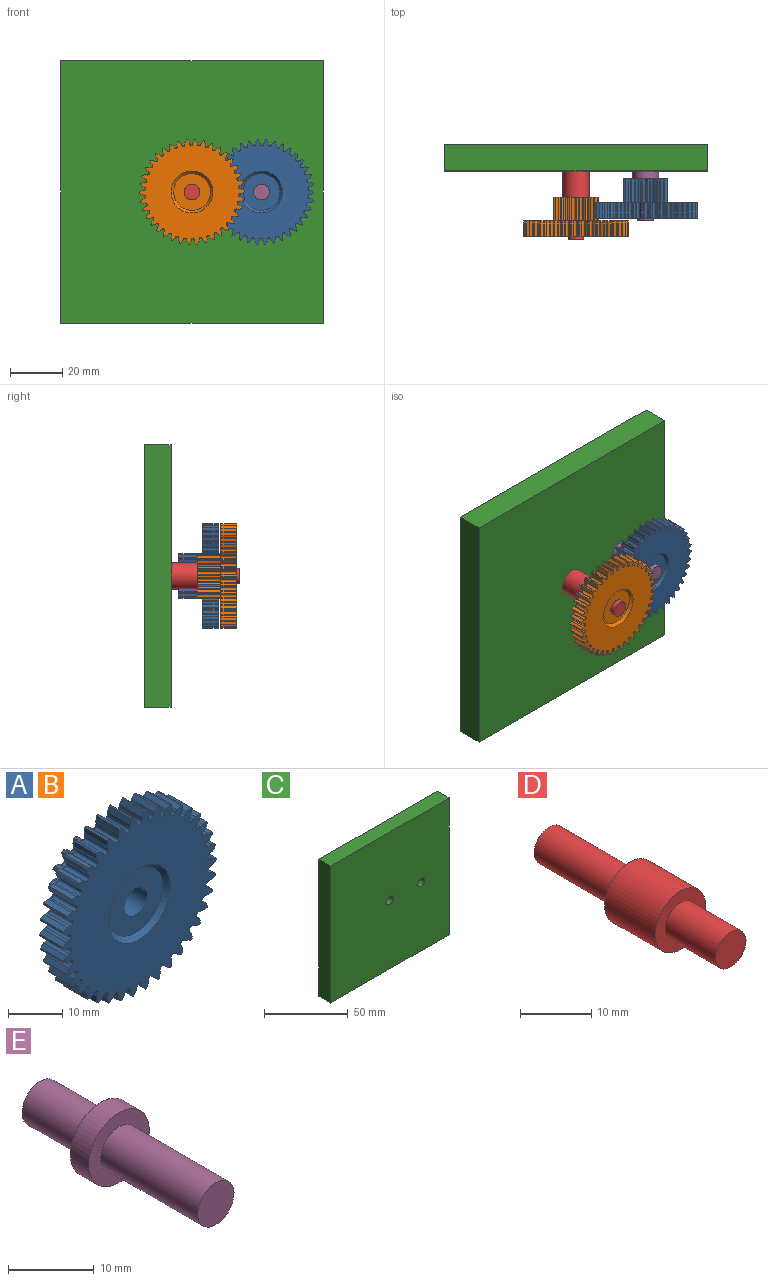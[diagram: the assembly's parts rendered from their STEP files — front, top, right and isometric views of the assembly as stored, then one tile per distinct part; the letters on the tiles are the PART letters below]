
ASSEMBLY  parts=5 mates=4
PART A: 326 faces, bbox 40x15x39.9 mm
  f0: plane 5x0.06mm, normal (-1,0,0), area 0.3mm2, adj f1,f3,f324
  f1: cylinder r=0.62mm len=5mm, axis (0,1,0), area 0.3mm2, adj f0,f3,f324
  f2: cylinder r=3mm len=14mm, axis (0,1,0), area 263.9mm2, adj f323,f324
  f3: plane 40x39.9mm, normal (0,1,0), area 943.4mm2, adj f0,f1,f4,f5,f6,f7,f8,f9
  f4: plane 6x0.6mm, normal (-0.33,0,-0.94), area 3.8mm2, adj f3,f5,f231,f232
  f5: cylinder r=0.62mm len=6mm, axis (0,1,0), area 11.7mm2, adj f3,f4,f6,f232
  f6: plane 6x0.63mm, normal (-0.19,0,0.98), area 3.9mm2, adj f3,f5,f7,f232
  f7: plane 6x1.02mm, normal (-0.51,0,0.86), area 7.1mm2, adj f3,f6,f8,f232
  f8: cylinder r=20mm len=6mm, axis (0,1,0), area 2.3mm2, adj f3,f7,f9,f232
  f9: plane 6x1.02mm, normal (-0.5,0,-0.87), area 7mm2, adj f3,f8,f10,f232
  f10: plane 6x0.63mm, normal (-0.17,0,-0.99), area 3.8mm2, adj f3,f9,f11,f232
  f11: cylinder r=0.62mm len=6mm, axis (0,1,0), area 11.7mm2, adj f3,f10,f12,f232
  f12: plane 6x0.6mm, normal (-0.35,0,0.94), area 3.9mm2, adj f3,f11,f13,f232
  f13: plane 6x0.9mm, normal (-0.65,0,0.76), area 7.1mm2, adj f3,f12,f14,f232
  f14: cylinder r=20mm len=6mm, axis (0,1,0), area 2.3mm2, adj f3,f13,f15,f232
  f15: plane 6x1.1mm, normal (-0.35,0,-0.94), area 7mm2, adj f3,f14,f16,f232
  f16: plane 6x0.64mm, normal (-0.01,0,-1), area 3.8mm2, adj f3,f15,f17,f232
  f17: cylinder r=0.62mm len=6mm, axis (0,1,0), area 11.7mm2, adj f3,f16,f18,f232
  f18: plane 6x0.56mm, normal (-0.5,0,0.87), area 3.9mm2, adj f3,f17,f19,f232
  f19: plane 6x0.9mm, normal (-0.76,0,0.65), area 7.1mm2, adj f3,f18,f20,f232
  f20: cylinder r=20mm len=6mm, axis (0,1,0), area 2.3mm2, adj f3,f19,f21,f232
  f21: plane 6x1.15mm, normal (-0.19,0,-0.98), area 7mm2, adj f3,f20,f22,f232
  f22: plane 6x0.63mm, normal (0.16,0,-0.99), area 3.8mm2, adj f3,f21,f23,f232
  f23: cylinder r=0.62mm len=6mm, axis (0,1,0), area 11.7mm2, adj f3,f22,f24,f232
  f24: plane 6x0.5mm, normal (-0.63,0,0.78), area 3.9mm2, adj f3,f23,f25,f232
  f25: plane 6x1.01mm, normal (-0.86,0,0.51), area 7.1mm2, adj f3,f24,f26,f232
  f26: cylinder r=20mm len=6mm, axis (0,1,0), area 2.3mm2, adj f3,f25,f27,f232
  f27: plane 6x1.17mm, normal (-0.02,0,-1), area 7mm2, adj f3,f26,f28,f232
  f28: plane 6x0.61mm, normal (0.32,0,-0.95), area 3.8mm2, adj f3,f27,f29,f232
  f29: cylinder r=0.62mm len=6mm, axis (0,1,0), area 11.7mm2, adj f3,f28,f30,f232
  f30: plane 6x0.48mm, normal (-0.75,0,0.66), area 3.9mm2, adj f3,f29,f31,f232
  f31: plane 6x1.1mm, normal (-0.93,0,0.36), area 7.1mm2, adj f3,f30,f32,f232
  f32: cylinder r=20mm len=6mm, axis (0,1,0), area 2.3mm2, adj f3,f31,f33,f232
  f33: plane 6x1.16mm, normal (0.14,0,-0.99), area 7mm2, adj f3,f32,f34,f232
  f34: plane 6x0.56mm, normal (0.47,0,-0.88), area 3.8mm2, adj f3,f33,f35,f232
  f35: cylinder r=0.62mm len=6mm, axis (0,1,0), area 11.7mm2, adj f3,f34,f36,f232
  f36: plane 6x0.55mm, normal (-0.85,0,0.53), area 3.9mm2, adj f3,f35,f37,f232
  f37: plane 6x1.16mm, normal (-0.98,0,0.21), area 7.1mm2, adj f3,f36,f38,f232
  f38: cylinder r=20mm len=6mm, axis (0,1,0), area 2.3mm2, adj f3,f37,f39,f232
  f39: plane 6x1.11mm, normal (0.3,0,-0.95), area 7mm2, adj f3,f38,f40,f232
  f40: plane 6x0.51mm, normal (0.61,0,-0.79), area 3.8mm2, adj f3,f39,f41,f232
  f41: cylinder r=0.62mm len=6mm, axis (0,1,0), area 11.7mm2, adj f3,f40,f42,f232
  f42: plane 6x0.59mm, normal (-0.92,0,0.38), area 3.9mm2, adj f3,f41,f43,f232
  f43: plane 6x1.18mm, normal (-1,0,0.04), area 7.1mm2, adj f3,f42,f44,f232
  f44: cylinder r=20mm len=6mm, axis (0,1,0), area 2.3mm2, adj f3,f43,f45,f232
  f45: plane 6x1.04mm, normal (0.46,0,-0.89), area 7mm2, adj f3,f44,f46,f232
  f46: plane 6x0.47mm, normal (0.73,0,-0.68), area 3.8mm2, adj f3,f45,f47,f232
  f47: cylinder r=0.62mm len=6mm, axis (0,1,0), area 11.7mm2, adj f3,f46,f48,f232
  f48: plane 6x0.63mm, normal (-0.97,0,0.22), area 3.9mm2, adj f3,f47,f49,f232
  f49: plane 6x1.17mm, normal (-0.99,0,-0.12), area 7.1mm2, adj f3,f48,f50,f232
  f50: cylinder r=20mm len=6mm, axis (0,1,0), area 2.3mm2, adj f3,f49,f51,f232
  f51: plane 6x0.94mm, normal (0.6,0,-0.8), area 7mm2, adj f3,f50,f52,f232
  f52: plane 6x0.53mm, normal (0.83,0,-0.55), area 3.8mm2, adj f3,f51,f53,f232
  f53: cylinder r=0.62mm len=6mm, axis (0,1,0), area 11.7mm2, adj f3,f52,f54,f232
  f54: plane 6x0.64mm, normal (-1,0,0.06), area 3.9mm2, adj f3,f53,f55,f232
  f55: plane 6x1.13mm, normal (-0.96,0,-0.28), area 7.1mm2, adj f3,f54,f56,f232
  f56: cylinder r=20mm len=6mm, axis (0,1,0), area 2.3mm2, adj f3,f55,f57,f232
  f57: plane 6x0.84mm, normal (0.72,0,-0.69), area 7mm2, adj f3,f56,f58,f232
  f58: plane 6x0.58mm, normal (0.91,0,-0.41), area 3.8mm2, adj f3,f57,f59,f232
  f59: cylinder r=0.62mm len=6mm, axis (0,1,0), area 11.7mm2, adj f3,f58,f60,f232
  f60: plane 6x0.64mm, normal (-0.99,0,-0.1), area 3.9mm2, adj f3,f59,f61,f232
  f61: plane 6x1.06mm, normal (-0.9,0,-0.44), area 7.1mm2, adj f3,f60,f62,f232
  f62: cylinder r=20mm len=6mm, axis (0,1,0), area 2.3mm2, adj f3,f61,f63,f232
  f63: plane 6x0.96mm, normal (0.82,0,-0.57), area 7mm2, adj f3,f62,f64,f232
  f64: plane 6x0.62mm, normal (0.97,0,-0.25), area 3.8mm2, adj f3,f63,f65,f232
  f65: cylinder r=0.62mm len=6mm, axis (0,1,0), area 11.7mm2, adj f3,f64,f66,f232
  f66: plane 6x0.62mm, normal (-0.96,0,-0.27), area 3.9mm2, adj f3,f65,f67,f232
  f67: plane 6x0.96mm, normal (-0.81,0,-0.58), area 7.1mm2, adj f3,f66,f68,f232
  f68: cylinder r=20mm len=6mm, axis (0,1,0), area 2.3mm2, adj f3,f67,f69,f232
  f69: plane 6x1.06mm, normal (0.91,0,-0.42), area 7mm2, adj f3,f68,f70,f232
  f70: plane 6x0.64mm, normal (1,0,-0.09), area 3.8mm2, adj f3,f69,f71,f232
  f71: cylinder r=0.62mm len=6mm, axis (0,1,0), area 11.7mm2, adj f3,f70,f72,f232
  f72: plane 6x0.58mm, normal (-0.91,0,-0.42), area 3.9mm2, adj f3,f71,f73,f232
  f73: plane 6x0.84mm, normal (-0.71,0,-0.71), area 7.1mm2, adj f3,f72,f74,f232
  f74: cylinder r=20mm len=6mm, axis (0,1,0), area 2.3mm2, adj f3,f73,f75,f232
  f75: plane 6x1.13mm, normal (0.96,0,-0.27), area 7mm2, adj f3,f74,f76,f232
  f76: plane 6x0.64mm, normal (1,0,0.08), area 3.8mm2, adj f3,f75,f77,f232
  f77: cylinder r=0.62mm len=6mm, axis (0,1,0), area 11.7mm2, adj f3,f76,f78,f232
  f78: plane 6x0.53mm, normal (-0.82,0,-0.57), area 3.9mm2, adj f3,f77,f79,f232
  f79: plane 6x0.96mm, normal (-0.58,0,-0.81), area 7.1mm2, adj f3,f78,f80,f232
  f80: cylinder r=20mm len=6mm, axis (0,1,0), area 2.3mm2, adj f3,f79,f81,f232
  f81: plane 6x1.16mm, normal (0.99,0,-0.11), area 7mm2, adj f3,f80,f82,f232
  f82: plane 6x0.62mm, normal (0.97,0,0.24), area 3.8mm2, adj f3,f81,f83,f232
  f83: cylinder r=0.62mm len=6mm, axis (0,1,0), area 11.7mm2, adj f3,f82,f84,f232
  f84: plane 6x0.46mm, normal (-0.72,0,-0.69), area 3.9mm2, adj f3,f83,f85,f232
  f85: plane 6x1.06mm, normal (-0.44,0,-0.9), area 7.1mm2, adj f3,f84,f86,f232
  f86: cylinder r=20mm len=6mm, axis (0,1,0), area 2.3mm2, adj f3,f85,f87,f232
  f87: plane 6x1.17mm, normal (1,0,0.06), area 7mm2, adj f3,f86,f88,f232
  f88: plane 6x0.59mm, normal (0.92,0,0.4), area 3.8mm2, adj f3,f87,f89,f232
  f89: cylinder r=0.62mm len=6mm, axis (0,1,0), area 11.7mm2, adj f3,f88,f90,f232
  f90: plane 6x0.52mm, normal (-0.6,0,-0.8), area 3.9mm2, adj f3,f89,f91,f232
  f91: plane 6x1.13mm, normal (-0.29,0,-0.96), area 7.1mm2, adj f3,f90,f92,f232
  f92: cylinder r=20mm len=6mm, axis (0,1,0), area 2.3mm2, adj f3,f91,f93,f232
  f93: plane 6x1.14mm, normal (0.97,0,0.22), area 7mm2, adj f3,f92,f94,f232
  f94: plane 6x0.54mm, normal (0.84,0,0.54), area 3.8mm2, adj f3,f93,f95,f232
  f95: cylinder r=0.62mm len=6mm, axis (0,1,0), area 11.7mm2, adj f3,f94,f96,f232
  f96: plane 6x0.57mm, normal (-0.46,0,-0.89), area 3.9mm2, adj f3,f95,f97,f232
  f97: plane 6x1.17mm, normal (-0.12,0,-0.99), area 7.1mm2, adj f3,f96,f98,f232
  f98: cylinder r=20mm len=6mm, axis (0,1,0), area 2.3mm2, adj f3,f97,f99,f232
  f99: plane 6x1.08mm, normal (0.92,0,0.38), area 7mm2, adj f3,f98,f100,f232
  f100: plane 6x0.47mm, normal (0.74,0,0.67), area 3.8mm2, adj f3,f99,f101,f232
  f101: cylinder r=0.62mm len=6mm, axis (0,1,0), area 11.7mm2, adj f3,f100,f102,f232
  f102: plane 6x0.61mm, normal (-0.3,0,-0.95), area 3.9mm2, adj f3,f101,f103,f232
  f103: plane 6x1.18mm, normal (0.04,0,-1), area 7.1mm2, adj f3,f102,f104,f232
  f104: cylinder r=20mm len=6mm, axis (0,1,0), area 2.3mm2, adj f3,f103,f105,f232
  f105: plane 6x0.99mm, normal (0.85,0,0.53), area 7mm2, adj f3,f104,f106,f232
  f106: plane 6x0.5mm, normal (0.62,0,0.79), area 3.8mm2, adj f3,f105,f107,f232
  f107: cylinder r=0.62mm len=6mm, axis (0,1,0), area 11.7mm2, adj f3,f106,f108,f232
  f108: plane 6x0.64mm, normal (-0.14,0,-0.99), area 3.9mm2, adj f3,f107,f109,f232
  f109: plane 6x1.16mm, normal (0.2,0,-0.98), area 7.1mm2, adj f3,f108,f110,f232
  f110: cylinder r=20mm len=6mm, axis (0,1,0), area 2.3mm2, adj f3,f109,f111,f232
  f111: plane 6x0.88mm, normal (0.75,0,0.66), area 7mm2, adj f3,f110,f112,f232
  f112: plane 6x0.56mm, normal (0.48,0,0.88), area 3.8mm2, adj f3,f111,f113,f232
  f113: cylinder r=0.62mm len=6mm, axis (0,1,0), area 11.7mm2, adj f3,f112,f114,f232
  f114: plane 6x0.64mm, normal (0.02,0,-1), area 3.9mm2, adj f3,f113,f115,f232
  f115: plane 6x1.1mm, normal (0.36,0,-0.93), area 7.1mm2, adj f3,f114,f116,f232
  f116: cylinder r=20mm len=6mm, axis (0,1,0), area 2.3mm2, adj f3,f115,f117,f232
  f117: plane 6x0.91mm, normal (0.63,0,0.77), area 7mm2, adj f3,f116,f118,f232
  f118: plane 6x0.6mm, normal (0.33,0,0.94), area 3.8mm2, adj f3,f117,f119,f232
  f119: cylinder r=0.62mm len=6mm, axis (0,1,0), area 11.7mm2, adj f3,f118,f120,f232
  f120: plane 6x0.63mm, normal (0.19,0,-0.98), area 3.9mm2, adj f3,f119,f121,f232
  f121: plane 6x1.02mm, normal (0.51,0,-0.86), area 7.1mm2, adj f3,f120,f122,f232
  f122: cylinder r=20mm len=6mm, axis (0,1,0), area 2.3mm2, adj f3,f121,f123,f232
  f123: plane 6x1.02mm, normal (0.5,0,0.87), area 7mm2, adj f3,f122,f124,f232
  f124: plane 6x0.63mm, normal (0.17,0,0.99), area 3.8mm2, adj f3,f123,f125,f232
  f125: cylinder r=0.62mm len=6mm, axis (0,1,0), area 11.7mm2, adj f3,f124,f126,f232
  f126: plane 6x0.6mm, normal (0.35,0,-0.94), area 3.9mm2, adj f3,f125,f127,f232
  f127: plane 6x0.9mm, normal (0.65,0,-0.76), area 7.1mm2, adj f3,f126,f128,f232
  f128: cylinder r=20mm len=6mm, axis (0,1,0), area 2.3mm2, adj f3,f127,f129,f232
  f129: plane 6x1.1mm, normal (0.35,0,0.94), area 7mm2, adj f3,f128,f130,f232
  f130: plane 6x0.64mm, normal (0.01,0,1), area 3.8mm2, adj f3,f129,f131,f232
  f131: cylinder r=0.62mm len=6mm, axis (0,1,0), area 11.7mm2, adj f3,f130,f132,f232
  f132: plane 6x0.56mm, normal (0.5,0,-0.87), area 3.9mm2, adj f3,f131,f133,f232
  f133: plane 6x0.9mm, normal (0.76,0,-0.65), area 7.1mm2, adj f3,f132,f134,f232
  f134: cylinder r=20mm len=6mm, axis (0,1,0), area 2.3mm2, adj f3,f133,f135,f232
  f135: plane 6x1.15mm, normal (0.19,0,0.98), area 7mm2, adj f3,f134,f136,f232
  f136: plane 6x0.63mm, normal (-0.16,0,0.99), area 3.8mm2, adj f3,f135,f137,f232
  f137: cylinder r=0.62mm len=6mm, axis (0,1,0), area 11.7mm2, adj f3,f136,f138,f232
  f138: plane 6x0.5mm, normal (0.63,0,-0.78), area 3.9mm2, adj f3,f137,f139,f232
  f139: plane 6x1.01mm, normal (0.86,0,-0.51), area 7.1mm2, adj f3,f138,f140,f232
  f140: cylinder r=20mm len=6mm, axis (0,1,0), area 2.3mm2, adj f3,f139,f141,f232
  f141: plane 6x1.17mm, normal (0.02,0,1), area 7mm2, adj f3,f140,f142,f232
  f142: plane 6x0.61mm, normal (-0.32,0,0.95), area 3.8mm2, adj f3,f141,f143,f232
  f143: cylinder r=0.62mm len=6mm, axis (0,1,0), area 11.7mm2, adj f3,f142,f144,f232
  f144: plane 6x0.48mm, normal (0.75,0,-0.66), area 3.9mm2, adj f3,f143,f145,f232
  f145: plane 6x1.1mm, normal (0.93,0,-0.36), area 7.1mm2, adj f3,f144,f146,f232
  f146: cylinder r=20mm len=6mm, axis (0,1,0), area 2.3mm2, adj f3,f145,f147,f232
  f147: plane 6x1.16mm, normal (-0.14,0,0.99), area 7mm2, adj f3,f146,f148,f232
  f148: plane 6x0.56mm, normal (-0.47,0,0.88), area 3.8mm2, adj f3,f147,f149,f232
  f149: cylinder r=0.62mm len=6mm, axis (0,1,0), area 11.7mm2, adj f3,f148,f150,f232
  f150: plane 6x0.55mm, normal (0.85,0,-0.53), area 3.9mm2, adj f3,f149,f151,f232
  f151: plane 6x1.16mm, normal (0.98,0,-0.21), area 7.1mm2, adj f3,f150,f152,f232
  f152: cylinder r=20mm len=6mm, axis (0,1,0), area 2.3mm2, adj f3,f151,f153,f232
  f153: plane 6x1.11mm, normal (-0.3,0,0.95), area 7mm2, adj f3,f152,f154,f232
  f154: plane 6x0.51mm, normal (-0.61,0,0.79), area 3.8mm2, adj f3,f153,f155,f232
  f155: cylinder r=0.62mm len=6mm, axis (0,1,0), area 11.7mm2, adj f3,f154,f156,f232
  f156: plane 6x0.59mm, normal (0.92,0,-0.38), area 3.9mm2, adj f3,f155,f157,f232
  f157: plane 6x1.18mm, normal (1,0,-0.04), area 7.1mm2, adj f3,f156,f158,f232
  f158: cylinder r=20mm len=6mm, axis (0,1,0), area 2.3mm2, adj f3,f157,f159,f232
  f159: plane 6x1.04mm, normal (-0.46,0,0.89), area 7mm2, adj f3,f158,f160,f232
  f160: plane 6x0.47mm, normal (-0.73,0,0.68), area 3.8mm2, adj f3,f159,f161,f232
  f161: cylinder r=0.62mm len=6mm, axis (0,1,0), area 11.7mm2, adj f3,f160,f162,f232
  f162: plane 6x0.63mm, normal (0.97,0,-0.22), area 3.9mm2, adj f3,f161,f163,f232
  f163: plane 6x1.17mm, normal (0.99,0,0.12), area 7.1mm2, adj f3,f162,f164,f232
  f164: cylinder r=20mm len=6mm, axis (0,1,0), area 2.3mm2, adj f3,f163,f165,f232
  f165: plane 6x0.94mm, normal (-0.6,0,0.8), area 7mm2, adj f3,f164,f166,f232
  f166: plane 6x0.53mm, normal (-0.83,0,0.55), area 3.8mm2, adj f3,f165,f167,f232
  f167: cylinder r=0.62mm len=6mm, axis (0,1,0), area 11.7mm2, adj f3,f166,f168,f232
  f168: plane 6x0.64mm, normal (1,0,-0.06), area 3.9mm2, adj f3,f167,f169,f232
  f169: plane 6x1.13mm, normal (0.96,0,0.28), area 7.1mm2, adj f3,f168,f170,f232
  f170: cylinder r=20mm len=6mm, axis (0,1,0), area 2.3mm2, adj f3,f169,f171,f232
  f171: plane 6x0.84mm, normal (-0.72,0,0.69), area 7mm2, adj f3,f170,f172,f232
  f172: plane 6x0.58mm, normal (-0.91,0,0.41), area 3.8mm2, adj f3,f171,f173,f232
  f173: cylinder r=0.62mm len=6mm, axis (0,1,0), area 11.7mm2, adj f3,f172,f174,f232
  f174: plane 6x0.64mm, normal (0.99,0,0.1), area 3.9mm2, adj f3,f173,f175,f232
  f175: plane 6x1.06mm, normal (0.9,0,0.44), area 7.1mm2, adj f3,f174,f176,f232
  f176: cylinder r=20mm len=6mm, axis (0,1,0), area 2.3mm2, adj f3,f175,f177,f232
  f177: plane 6x0.96mm, normal (-0.82,0,0.57), area 7mm2, adj f3,f176,f178,f232
  f178: plane 6x0.62mm, normal (-0.97,0,0.25), area 3.8mm2, adj f3,f177,f179,f232
  f179: cylinder r=0.62mm len=6mm, axis (0,1,0), area 11.7mm2, adj f3,f178,f180,f232
  f180: plane 6x0.62mm, normal (0.96,0,0.27), area 3.9mm2, adj f3,f179,f181,f232
  f181: plane 6x0.96mm, normal (0.81,0,0.58), area 7.1mm2, adj f3,f180,f182,f232
  f182: cylinder r=20mm len=6mm, axis (0,1,0), area 2.3mm2, adj f3,f181,f183,f232
  f183: plane 6x1.06mm, normal (-0.91,0,0.42), area 7mm2, adj f3,f182,f184,f232
  f184: plane 6x0.64mm, normal (-1,0,0.09), area 3.8mm2, adj f3,f183,f185,f232
  f185: cylinder r=0.62mm len=6mm, axis (0,1,0), area 11.7mm2, adj f3,f184,f186,f232
  f186: plane 6x0.58mm, normal (0.91,0,0.42), area 3.9mm2, adj f3,f185,f187,f232
  f187: plane 6x0.84mm, normal (0.71,0,0.71), area 7.1mm2, adj f3,f186,f188,f232
  f188: cylinder r=20mm len=6mm, axis (0,1,0), area 2.3mm2, adj f3,f187,f189,f232
  f189: plane 6x1.13mm, normal (-0.96,0,0.27), area 7mm2, adj f3,f188,f190,f232
  f190: plane 6x0.64mm, normal (-1,0,-0.08), area 3.8mm2, adj f3,f189,f191,f232
  f191: cylinder r=0.62mm len=6mm, axis (0,1,0), area 11.7mm2, adj f3,f190,f192,f232
  f192: plane 6x0.53mm, normal (0.82,0,0.57), area 3.9mm2, adj f3,f191,f193,f232
  f193: plane 6x0.96mm, normal (0.58,0,0.81), area 7.1mm2, adj f3,f192,f194,f232
  f194: cylinder r=20mm len=6mm, axis (0,1,0), area 2.3mm2, adj f3,f193,f195,f232
  f195: plane 6x1.16mm, normal (-0.99,0,0.11), area 7mm2, adj f3,f194,f196,f232
  f196: plane 6x0.62mm, normal (-0.97,0,-0.24), area 3.8mm2, adj f3,f195,f197,f232
  f197: cylinder r=0.62mm len=6mm, axis (0,1,0), area 11.7mm2, adj f3,f196,f198,f232
  f198: plane 6x0.46mm, normal (0.72,0,0.69), area 3.9mm2, adj f3,f197,f199,f232
  f199: plane 6x1.06mm, normal (0.44,0,0.9), area 7.1mm2, adj f3,f198,f200,f232
  f200: cylinder r=20mm len=6mm, axis (0,1,0), area 2.3mm2, adj f3,f199,f201,f232
  f201: plane 6x1.17mm, normal (-1,0,-0.06), area 7mm2, adj f3,f200,f202,f232
  f202: plane 6x0.59mm, normal (-0.92,0,-0.4), area 3.8mm2, adj f3,f201,f203,f232
  f203: cylinder r=0.62mm len=6mm, axis (0,1,0), area 11.7mm2, adj f3,f202,f204,f232
  f204: plane 6x0.52mm, normal (0.6,0,0.8), area 3.9mm2, adj f3,f203,f205,f232
  f205: plane 6x1.13mm, normal (0.29,0,0.96), area 7.1mm2, adj f3,f204,f206,f232
  f206: cylinder r=20mm len=6mm, axis (0,1,0), area 2.3mm2, adj f3,f205,f207,f232
  f207: plane 6x1.14mm, normal (-0.97,0,-0.22), area 7mm2, adj f3,f206,f208,f232
  f208: plane 6x0.54mm, normal (-0.84,0,-0.54), area 3.8mm2, adj f3,f207,f209,f232
  f209: cylinder r=0.62mm len=6mm, axis (0,1,0), area 11.7mm2, adj f3,f208,f210,f232
  f210: plane 6x0.57mm, normal (0.46,0,0.89), area 3.9mm2, adj f3,f209,f211,f232
  f211: plane 6x1.17mm, normal (0.12,0,0.99), area 7.1mm2, adj f3,f210,f212,f232
  f212: cylinder r=20mm len=6mm, axis (0,1,0), area 2.3mm2, adj f3,f211,f213,f232
  f213: plane 6x1.08mm, normal (-0.92,0,-0.38), area 7mm2, adj f3,f212,f214,f232
  f214: plane 6x0.47mm, normal (-0.74,0,-0.67), area 3.8mm2, adj f3,f213,f215,f232
  f215: cylinder r=0.62mm len=6mm, axis (0,1,0), area 11.7mm2, adj f3,f214,f216,f232
  f216: plane 6x0.61mm, normal (0.3,0,0.95), area 3.9mm2, adj f3,f215,f217,f232
  f217: plane 6x1.18mm, normal (-0.04,0,1), area 7.1mm2, adj f3,f216,f218,f232
  f218: cylinder r=20mm len=6mm, axis (0,1,0), area 2.3mm2, adj f3,f217,f219,f232
  f219: plane 6x0.99mm, normal (-0.85,0,-0.53), area 7mm2, adj f3,f218,f220,f232
  f220: plane 6x0.5mm, normal (-0.62,0,-0.79), area 3.8mm2, adj f3,f219,f221,f232
  f221: cylinder r=0.62mm len=6mm, axis (0,1,0), area 11.7mm2, adj f3,f220,f222,f232
  f222: plane 6x0.64mm, normal (0.14,0,0.99), area 3.9mm2, adj f3,f221,f223,f232
  f223: plane 6x1.16mm, normal (-0.2,0,0.98), area 7.1mm2, adj f3,f222,f224,f232
  f224: cylinder r=20mm len=6mm, axis (0,1,0), area 2.3mm2, adj f3,f223,f225,f232
  f225: plane 6x0.88mm, normal (-0.75,0,-0.66), area 7mm2, adj f3,f224,f226,f232
  f226: plane 6x0.56mm, normal (-0.48,0,-0.88), area 3.8mm2, adj f3,f225,f227,f232
  f227: cylinder r=0.62mm len=6mm, axis (0,1,0), area 11.7mm2, adj f3,f226,f228,f232
  f228: plane 6x0.64mm, normal (-0.02,0,1), area 3.9mm2, adj f3,f227,f229,f232
  f229: plane 6x1.1mm, normal (-0.36,0,0.93), area 7.1mm2, adj f3,f228,f230,f232
  f230: cylinder r=20mm len=6mm, axis (0,1,0), area 2.3mm2, adj f3,f229,f231,f232
  f231: plane 6x0.91mm, normal (-0.63,0,-0.77), area 7mm2, adj f3,f4,f230,f232
  f232: plane 40x39.9mm, normal (0,-1,0), area 913mm2, adj f4,f5,f6,f7,f8,f9,f10,f11
  f233: cylinder r=0.62mm len=9mm, axis (0,-1,0), area 17.2mm2, adj f3,f234,f322,f323
  f234: plane 9x0.62mm, normal (0.99,0,-0.17), area 5.7mm2, adj f3,f233,f235,f323
  f235: plane 9x1.1mm, normal (0.98,0,0.18), area 10.1mm2, adj f3,f234,f236,f323
  f236: cylinder r=8.5mm len=9mm, axis (0,-1,0), area 5.7mm2, adj f3,f235,f237,f323
  f237: plane 9x0.91mm, normal (-0.8,0,0.6), area 10.3mm2, adj f3,f236,f238,f323
  f238: plane 9x0.61mm, normal (-0.96,0,0.29), area 5.7mm2, adj f3,f237,f239,f323
  f239: cylinder r=0.62mm len=9mm, axis (0,-1,0), area 17.2mm2, adj f3,f238,f240,f323
  f240: plane 9x0.61mm, normal (0.97,0,0.25), area 5.7mm2, adj f3,f239,f241,f323
  f241: plane 9x0.92mm, normal (0.82,0,0.57), area 10.1mm2, adj f3,f240,f242,f323
  f242: cylinder r=8.5mm len=9mm, axis (0,-1,0), area 5.7mm2, adj f3,f241,f243,f323
  f243: plane 9x1.11mm, normal (-0.97,0,0.23), area 10.3mm2, adj f3,f242,f244,f323
  f244: plane 9x0.63mm, normal (-0.99,0,-0.12), area 5.7mm2, adj f3,f243,f245,f323
  f245: cylinder r=0.62mm len=9mm, axis (0,-1,0), area 17.2mm2, adj f3,f244,f246,f323
  f246: plane 9x0.5mm, normal (0.78,0,0.62), area 5.7mm2, adj f3,f245,f247,f323
  f247: plane 9x0.95mm, normal (0.52,0,0.85), area 10.1mm2, adj f3,f246,f248,f323
  f248: cylinder r=8.5mm len=9mm, axis (0,-1,0), area 5.7mm2, adj f3,f247,f249,f323
  f249: plane 9x1.12mm, normal (-0.98,0,-0.19), area 10.3mm2, adj f3,f248,f250,f323
  f250: plane 9x0.55mm, normal (-0.86,0,-0.51), area 5.7mm2, adj f3,f249,f251,f323
  f251: cylinder r=0.62mm len=9mm, axis (0,-1,0), area 17.2mm2, adj f3,f250,f252,f323
  f252: plane 9x0.56mm, normal (0.46,0,0.89), area 5.7mm2, adj f3,f251,f253,f323
  f253: plane 9x1.11mm, normal (0.13,0,0.99), area 10.1mm2, adj f3,f252,f254,f323
  f254: cylinder r=8.5mm len=9mm, axis (0,-1,0), area 5.7mm2, adj f3,f253,f255,f323
  f255: plane 9x0.94mm, normal (-0.82,0,-0.57), area 10.3mm2, adj f3,f254,f256,f323
  f256: plane 9x0.52mm, normal (-0.58,0,-0.82), area 5.7mm2, adj f3,f255,f257,f323
  f257: cylinder r=0.62mm len=9mm, axis (0,-1,0), area 17.2mm2, adj f3,f256,f258,f323
  f258: plane 9x0.63mm, normal (0.06,0,1), area 5.7mm2, adj f3,f257,f259,f323
  f259: plane 9x1.07mm, normal (-0.28,0,0.96), area 10.1mm2, adj f3,f258,f260,f323
  f260: cylinder r=8.5mm len=9mm, axis (0,-1,0), area 5.7mm2, adj f3,f259,f261,f323
  f261: plane 9x0.98mm, normal (-0.52,0,-0.86), area 10.3mm2, adj f3,f260,f262,f323
  f262: plane 9x0.63mm, normal (-0.19,0,-0.98), area 5.7mm2, adj f3,f261,f263,f323
  f263: cylinder r=0.62mm len=9mm, axis (0,-1,0), area 17.2mm2, adj f3,f262,f264,f323
  f264: plane 9x0.59mm, normal (-0.35,0,0.94), area 5.7mm2, adj f3,f263,f265,f323
  f265: plane 9x0.85mm, normal (-0.65,0,0.76), area 10.1mm2, adj f3,f264,f266,f323
  f266: cylinder r=8.5mm len=9mm, axis (0,-1,0), area 5.7mm2, adj f3,f265,f267,f323
  f267: plane 9x1.13mm, normal (-0.12,0,-0.99), area 10.3mm2, adj f3,f266,f268,f323
  f268: plane 9x0.62mm, normal (0.22,0,-0.97), area 5.7mm2, adj f3,f267,f269,f323
  f269: cylinder r=0.62mm len=9mm, axis (0,-1,0), area 17.2mm2, adj f3,f268,f270,f323
  f270: plane 9x0.45mm, normal (-0.7,0,0.71), area 5.7mm2, adj f3,f269,f271,f323
  f271: plane 9x1.01mm, normal (-0.9,0,0.43), area 10.1mm2, adj f3,f270,f272,f323
  f272: cylinder r=8.5mm len=9mm, axis (0,-1,0), area 5.7mm2, adj f3,f271,f273,f323
  f273: plane 9x1.09mm, normal (0.29,0,-0.96), area 10.3mm2, adj f3,f272,f274,f323
  f274: plane 9x0.51mm, normal (0.6,0,-0.8), area 5.7mm2, adj f3,f273,f275,f323
  f275: cylinder r=0.62mm len=9mm, axis (0,-1,0), area 17.2mm2, adj f3,f274,f276,f323
  f276: plane 9x0.59mm, normal (-0.93,0,0.37), area 5.7mm2, adj f3,f275,f277,f323
  f277: plane 9x1.12mm, normal (-1,0,0.03), area 10.1mm2, adj f3,f276,f278,f323
  f278: cylinder r=8.5mm len=9mm, axis (0,-1,0), area 5.7mm2, adj f3,f277,f279,f323
  f279: plane 9x0.86mm, normal (0.65,0,-0.76), area 10.3mm2, adj f3,f278,f280,f323
  f280: plane 9x0.56mm, normal (0.87,0,-0.49), area 5.7mm2, adj f3,f279,f281,f323
  f281: cylinder r=0.62mm len=9mm, axis (0,-1,0), area 17.2mm2, adj f3,f280,f282,f323
  f282: plane 9x0.63mm, normal (-1,0,-0.04), area 5.7mm2, adj f3,f281,f283,f323
  f283: plane 9x1.03mm, normal (-0.92,0,-0.38), area 10.1mm2, adj f3,f282,f284,f323
  f284: cylinder r=8.5mm len=9mm, axis (0,-1,0), area 5.7mm2, adj f3,f283,f285,f323
  f285: plane 9x1.03mm, normal (0.91,0,-0.42), area 10.3mm2, adj f3,f284,f286,f323
  f286: plane 9x0.64mm, normal (1,0,-0.09), area 5.7mm2, adj f3,f285,f287,f323
  f287: cylinder r=0.62mm len=9mm, axis (0,-1,0), area 17.2mm2, adj f3,f286,f288,f323
  f288: plane 9x0.57mm, normal (-0.89,0,-0.45), area 5.7mm2, adj f3,f287,f289,f323
  f289: plane 9x0.81mm, normal (-0.69,0,-0.73), area 10.1mm2, adj f3,f288,f290,f323
  f290: cylinder r=8.5mm len=9mm, axis (0,-1,0), area 5.7mm2, adj f3,f289,f291,f323
  f291: plane 9x1.14mm, normal (1,0,-0.02), area 10.3mm2, adj f3,f290,f292,f323
  f292: plane 9x0.6mm, normal (0.95,0,0.32), area 5.7mm2, adj f3,f291,f293,f323
  f293: cylinder r=0.62mm len=9mm, axis (0,-1,0), area 17.2mm2, adj f3,f292,f294,f323
  f294: plane 9x0.49mm, normal (-0.64,0,-0.77), area 5.7mm2, adj f3,f293,f295,f323
  f295: plane 9x1.05mm, normal (-0.33,0,-0.94), area 10.1mm2, adj f3,f294,f296,f323
  f296: cylinder r=8.5mm len=9mm, axis (0,-1,0), area 5.7mm2, adj f3,f295,f297,f323
  f297: plane 9x1.05mm, normal (0.92,0,0.39), area 10.3mm2, adj f3,f296,f298,f323
  f298: plane 9x0.47mm, normal (0.73,0,0.68), area 5.7mm2, adj f3,f297,f299,f323
  f299: cylinder r=0.62mm len=9mm, axis (0,-1,0), area 17.2mm2, adj f3,f298,f300,f323
  f300: plane 9x0.61mm, normal (-0.27,0,-0.96), area 5.7mm2, adj f3,f299,f301,f323
  f301: plane 9x1.12mm, normal (0.08,0,-1), area 10.1mm2, adj f3,f300,f302,f323
  f302: cylinder r=8.5mm len=9mm, axis (0,-1,0), area 5.7mm2, adj f3,f301,f303,f323
  f303: plane 9x0.83mm, normal (0.68,0,0.73), area 10.3mm2, adj f3,f302,f304,f323
  f304: plane 9x0.59mm, normal (0.39,0,0.92), area 5.7mm2, adj f3,f303,f305,f323
  f305: cylinder r=0.62mm len=9mm, axis (0,-1,0), area 17.2mm2, adj f3,f304,f306,f323
  f306: plane 9x0.63mm, normal (0.15,0,-0.99), area 5.7mm2, adj f3,f305,f307,f323
  f307: plane 9x0.98mm, normal (0.48,0,-0.88), area 10.1mm2, adj f3,f306,f308,f323
  f308: cylinder r=8.5mm len=9mm, axis (0,-1,0), area 5.7mm2, adj f3,f307,f309,f323
  f309: plane 9x1.08mm, normal (0.33,0,0.94), area 10.3mm2, adj f3,f308,f310,f323
  f310: plane 9x0.64mm, normal (-0.02,0,1), area 5.7mm2, adj f3,f309,f311,f323
  f311: cylinder r=0.62mm len=9mm, axis (0,-1,0), area 17.2mm2, adj f3,f310,f312,f323
  f312: plane 9x0.53mm, normal (0.54,0,-0.84), area 5.7mm2, adj f3,f311,f313,f323
  f313: plane 9x0.89mm, normal (0.79,0,-0.61), area 10.1mm2, adj f3,f312,f314,f323
  f314: cylinder r=8.5mm len=9mm, axis (0,-1,0), area 5.7mm2, adj f3,f313,f315,f323
  f315: plane 9x1.14mm, normal (-0.09,0,1), area 10.3mm2, adj f3,f314,f316,f323
  f316: plane 9x0.58mm, normal (-0.42,0,0.91), area 5.7mm2, adj f3,f315,f317,f323
  f317: cylinder r=0.62mm len=9mm, axis (0,-1,0), area 17.2mm2, adj f3,f316,f318,f323
  f318: plane 9x0.53mm, normal (0.83,0,-0.55), area 5.7mm2, adj f3,f317,f319,f323
  f319: plane 9x1.09mm, normal (0.97,0,-0.23), area 10.1mm2, adj f3,f318,f320,f323
  f320: cylinder r=8.5mm len=9mm, axis (0,-1,0), area 5.7mm2, adj f3,f319,f321,f323
  f321: plane 9x1mm, normal (-0.48,0,0.88), area 10.3mm2, adj f3,f320,f322,f323
  f322: plane 9x0.48mm, normal (-0.75,0,0.66), area 5.7mm2, adj f3,f233,f321,f323
  f323: plane 16.96x16.88mm, normal (0,1,0), area 142.3mm2, adj f2,f233,f234,f235,f236,f237,f238,f239
  f324: plane 14x14mm, normal (0,-1,0), area 125.7mm2, adj f0,f1,f2,f325
  f325: cone r=7mm half-angle=45deg, axis (0,-1,0), area 66.6mm2, adj f232,f324
PART B: same geometry as A
PART C: 8 faces, bbox 100x10x100 mm
  f0: plane 100x10mm, normal (0,0,1), area 1000mm2, adj f1,f5,f6,f7
  f1: plane 100x10mm, normal (-1,0,0), area 1000mm2, adj f0,f2,f6,f7
  f2: plane 100x10mm, normal (0,0,-1), area 1000mm2, adj f1,f5,f6,f7
  f3: cylinder r=3mm len=10mm, axis (0,1,0), area 188.5mm2, adj f6,f7
  f4: cylinder r=3mm len=10mm, axis (0,1,0), area 188.5mm2, adj f6,f7
  f5: plane 100x10mm, normal (1,0,0), area 1000mm2, adj f0,f2,f6,f7
  f6: plane 100x100mm, normal (0,-1,0), area 9943.5mm2, adj f0,f1,f2,f3,f4,f5
  f7: plane 100x100mm, normal (0,1,0), area 9943.5mm2, adj f0,f1,f2,f3,f4,f5
PART D: 7 faces, bbox 10x36x10 mm
  f0: cylinder r=3mm len=10mm, axis (0,1,0), area 188.5mm2, adj f1,f4
  f1: plane 6x6mm, normal (0,-1,0), area 28.3mm2, adj f0
  f2: cylinder r=5mm len=10mm, axis (0,-1,0), area 314.2mm2, adj f3,f4
  f3: plane 10x10mm, normal (0,1,0), area 50.3mm2, adj f2,f5
  f4: plane 10x10mm, normal (0,-1,0), area 50.3mm2, adj f0,f2
  f5: cylinder r=3mm len=16mm, axis (0,-1,0), area 301.6mm2, adj f3,f6
  f6: plane 6x6mm, normal (0,1,0), area 28.3mm2, adj f5
PART E: 7 faces, bbox 10x29x10 mm
  f0: cylinder r=3mm len=10mm, axis (0,-1,0), area 188.5mm2, adj f1,f4
  f1: plane 6x6mm, normal (0,1,0), area 28.3mm2, adj f0
  f2: cylinder r=5mm len=10mm, axis (0,1,0), area 94.2mm2, adj f3,f4
  f3: plane 10x10mm, normal (0,-1,0), area 50.3mm2, adj f2,f5
  f4: plane 10x10mm, normal (0,1,0), area 50.3mm2, adj f0,f2
  f5: cylinder r=3mm len=16mm, axis (0,1,0), area 301.6mm2, adj f3,f6
  f6: plane 6x6mm, normal (0,-1,0), area 28.3mm2, adj f5
PLACE A rot(axis=(0,1,0),19.5deg) t=(76.5,-17.13,50)mm
PLACE B rot(axis=(0,1,0),160.1deg) t=(50,-24.13,50)mm
PLACE C t=(50,4.87,50)mm fixed
PLACE D rot(axis=(1,0,0),180deg) t=(50,-5.13,50)mm
PLACE E rot(axis=(0,-1,0),180deg) t=(76.5,-5.13,50)mm
MATE fastened D.f0 <-> C.f3  axis (0,1,0) through (50,4.87,50)mm
MATE revolute A.f2 <-> E.f5  axis (0,-1,0) through (76.5,-8.13,50)mm
MATE fastened E.f0 <-> C.f4  axis (0,1,0) through (76.5,4.87,50)mm
MATE revolute B.f2 <-> D.f2  axis (0,-1,0) through (50,-15.13,50)mm
